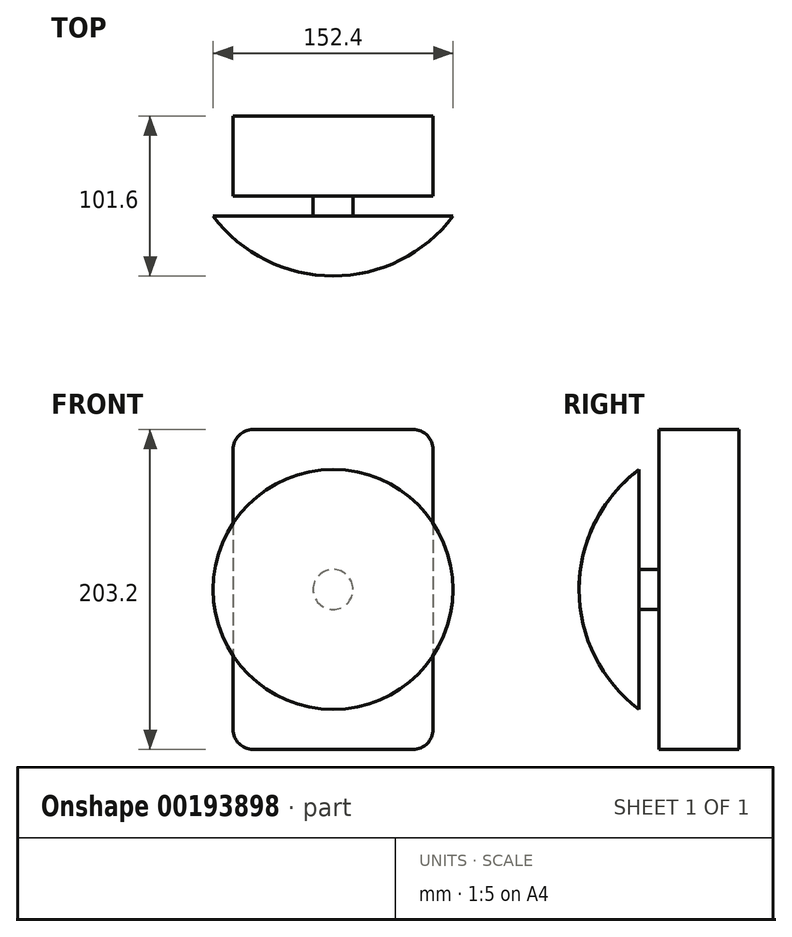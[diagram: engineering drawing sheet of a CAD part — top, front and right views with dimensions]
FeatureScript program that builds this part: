
annotation { "Feature Type Name" : "Feature", "Feature Type Description" : "" }
export const myFeature = defineFeature(function(context is Context, id is Id, definition is map)
    precondition{}
    {
        {
            var Q0;
            Q0=qCreatedBy(makeId("Front.planeOp"),FACE);
            var sketch = newSketch(context, id + "F0", { "sketchPlane" : qUnion([Q0])});
            skLineSegment(sketch, "E0.bottom", {"start": v(-63.5, 101.6) * mm, "end": v(63.5, 101.6) * mm});
            skLineSegment(sketch, "E0.top", {"start": v(-63.5, -101.6) * mm, "end": v(63.5, -101.6) * mm});
            skLineSegment(sketch, "E0.left", {"start": v(-63.5, 101.6) * mm, "end": v(-63.5, -101.6) * mm});
            skLineSegment(sketch, "E0.right", {"start": v(63.5, 101.6) * mm, "end": v(63.5, -101.6) * mm});
            skLineSegment(sketch, "E1", {"start": v(-63.5, 101.6) * mm, "end": v(63.5, -101.6) * mm, "construction": true});
            skPoint(sketch, "E2", {"position": v(0, 0) * mm});
            skSolve(sketch);
        }
        {
            var Q0;
            Q0 = qSketchRegion(id + "F0", true);
            extrude(context, id + "F1", {"entities" : qUnion([Q0]), "depth" : 50.8 * mm});
        }
        {
            var Q0;
            Q0=qCreatedBy(makeId("Right.planeOp"),FACE);
            var sketch = newSketch(context, id + "F2", { "sketchPlane" : qUnion([Q0])});
            skLineSegment(sketch, "E3", {"start": v(-50.8, 12.7) * mm, "end": v(-63.5, 12.7) * mm});
            skLineSegment(sketch, "E4", {"start": v(-63.5, 12.7) * mm, "end": v(-63.5, 76.2) * mm});
            skLineSegment(sketch, "E5", {"start": v(-50.8, 0) * mm, "end": v(-101.6, 0) * mm});
            skLineSegment(sketch, "E6", {"start": v(-50.8, 12.7) * mm, "end": v(-50.8, 0) * mm});
            skArc(sketch, "E7", {"start": v(-63.5, 76.2) * mm, "mid": v(-91.54, 42.6) * mm, "end": v(-101.6, 0) * mm});
            skLineSegment(sketch, "E8", {"start": v(-101.6, 0) * mm, "end": v(-101.6, 33.83) * mm, "construction": true});
            skSolve(sketch);
        }
        {
            var Q0;
            Q0=makeQuery(id+"F2.imprint","IMPRINT",FACE,{"disambiguationData":[TD([[makeQuery(id+"F2.imprint","IMPRINT",EDGE,{"derivedFrom":sQuery(id+"F2.wireOp",EDGE,"E3")}),1.0]])]});
            var Q1;
            Q1=sQuery(id+"F2.wireOp",EDGE,"E5");
            revolve(context, id + "F3", {"entities" : qUnion([Q0]), "axis" : qUnion([Q1]), "revolveType" : RevolveType.FULL});
        }
        {
            var Q0;
            Q0=makeQuery(id+"F1.opExtrude","SWEPT_EDGE",EDGE,{"disambiguationData":[OSD([sQuery(id+"F0.wireOp",EDGE,"E0.bottom"),sQuery(id+"F0.wireOp",EDGE,"E0.right")])]});
            var Q1;
            Q1=makeQuery(id+"F1.opExtrude","SWEPT_EDGE",EDGE,{"disambiguationData":[OSD([sQuery(id+"F0.wireOp",EDGE,"E0.bottom"),sQuery(id+"F0.wireOp",EDGE,"E0.left")])]});
            var Q2;
            Q2=makeQuery(id+"F1.opExtrude","SWEPT_EDGE",EDGE,{"disambiguationData":[OSD([sQuery(id+"F0.wireOp",EDGE,"E0.top"),sQuery(id+"F0.wireOp",EDGE,"E0.right")])]});
            var Q3;
            Q3=makeQuery(id+"F1.opExtrude","SWEPT_EDGE",EDGE,{"disambiguationData":[OSD([sQuery(id+"F0.wireOp",EDGE,"E0.top"),sQuery(id+"F0.wireOp",EDGE,"E0.left")])]});
            fillet(context, id + "F4", {"entities" : qUnion([Q0, Q1, Q2, Q3]), "radius" : 12.7 * mm, "tangentPropagation" : true, "allowEdgeOverflow" : false});
        }
    });
